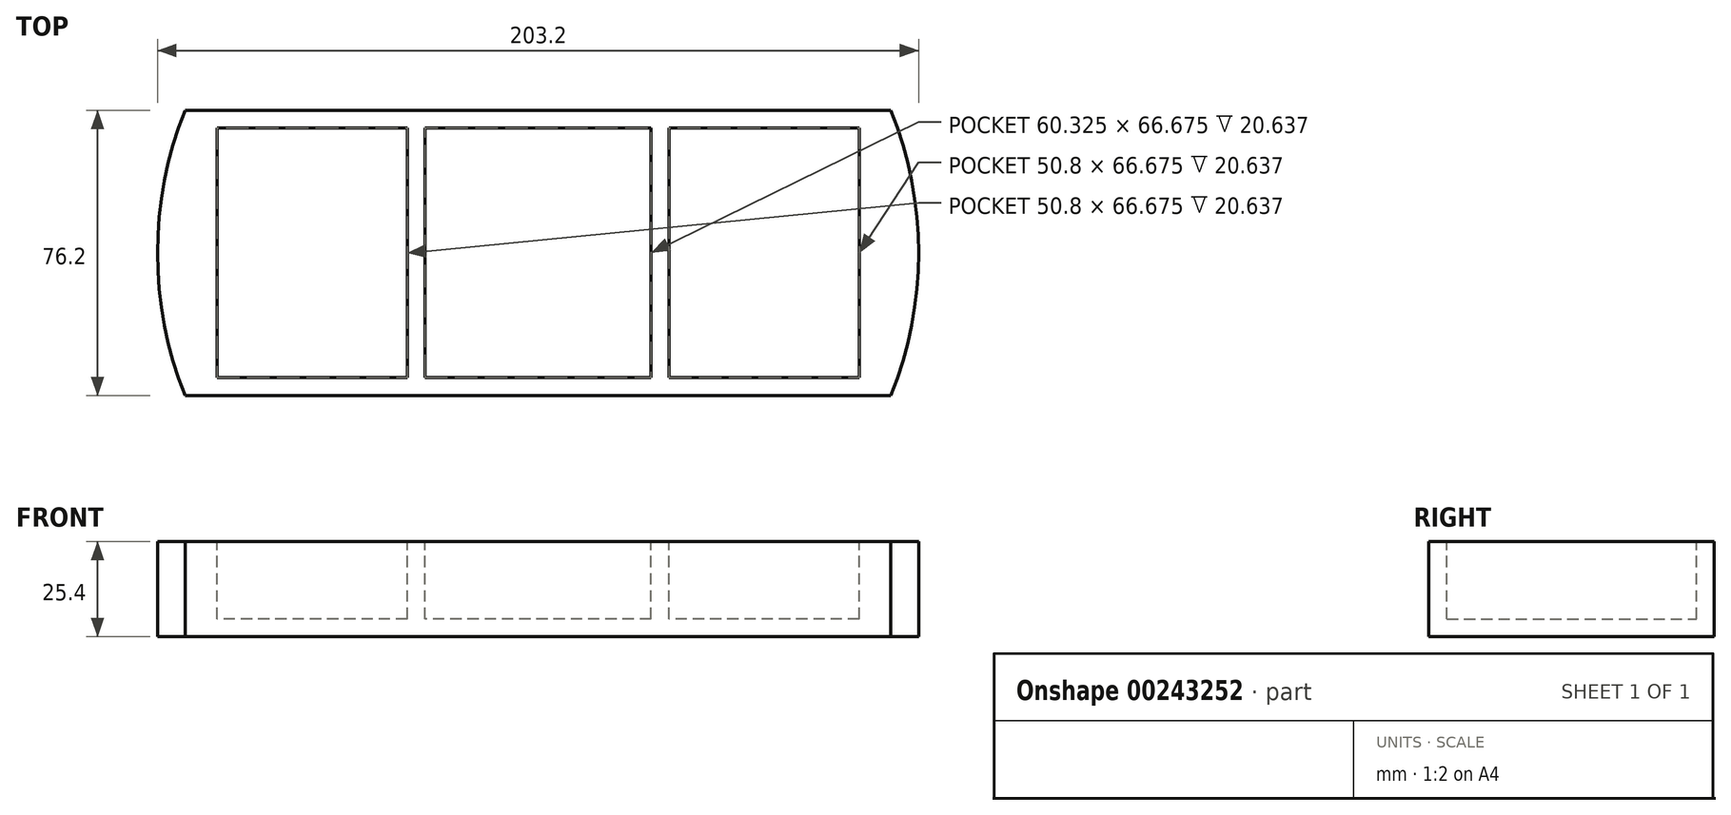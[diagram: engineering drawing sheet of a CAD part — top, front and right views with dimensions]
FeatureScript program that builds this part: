
annotation { "Feature Type Name" : "Feature", "Feature Type Description" : "" }
export const myFeature = defineFeature(function(context is Context, id is Id, definition is map)
    precondition{}
    {
        {
            var Q0;
            Q0=qCreatedBy(makeId("Front.planeOp"),FACE);
            var sketch = newSketch(context, id + "F0", { "sketchPlane" : qUnion([Q0])});
            skLineSegment(sketch, "E0.bottom", {"start": v(0, 0) * mm, "end": v(-203.2, 0) * mm});
            skLineSegment(sketch, "E0.top", {"start": v(0, 25.4) * mm, "end": v(-203.2, 25.4) * mm});
            skLineSegment(sketch, "E0.left", {"start": v(0, 0) * mm, "end": v(0, 25.4) * mm});
            skLineSegment(sketch, "E0.right", {"start": v(-203.2, 0) * mm, "end": v(-203.2, 25.4) * mm});
            skSolve(sketch);
        }
        {
            var Q0;
            Q0=makeQuery(id+"F0.imprint","IMPRINT",FACE,{"disambiguationData":[TD([[makeQuery(id+"F0.imprint","IMPRINT",EDGE,{"derivedFrom":sQuery(id+"F0.wireOp",EDGE,"E0.bottom")}),-1.0]])]});
            extrude(context, id + "F1", {"entities" : qUnion([Q0]), "depth" : 76.2 * mm});
        }
        {
            var Q0;
            Q0=makeQuery(id+"F1.opExtrude","SWEPT_FACE",FACE,{"disambiguationData":[OSD([sQuery(id+"F0.wireOp",EDGE,"E0.top")])]});
            var sketch = newSketch(context, id + "F2", { "sketchPlane" : qUnion([Q0])});
            skCircle(sketch, "E1", {"center": v(-101.6, -38.1) * mm, "radius": 101.6 * mm});
            skPoint(sketch, "E1.centerSnap0", {"position": v(-203.2, -38.1) * mm});
            skPoint(sketch, "E1.centerSnap1", {"position": v(-101.6, 0) * mm});
            skSolve(sketch);
        }
        {
            var Q0;
            {var subQ0=sQuery(id+"F2.wireOp",EDGE,"E1");var subQ1=sQuery(id+"F0.wireOp",EDGE,"E0.top");var subQ4=makeQuery(id+"F1.opExtrude","CAP_EDGE",EDGE,{"disambiguationData":[OSD([subQ1])],"isStart":false});var subQ5=makeQuery(id+"F2.imprint","INTERSECT",VERTEX,{"disambiguationData":[OD(1.0)],"derivedFrom":[subQ4,subQ0]});Q0=makeQuery(id+"F2.imprint","IMPRINT",FACE,{"disambiguationData":[TD([[makeQuery(id+"F2.imprint","IMPRINT",EDGE,{"disambiguationData":[TD([[subQ5,-1.0]])],"derivedFrom":subQ0}),-1.0]])]});}
            var Q1;
            {var subQ0=sQuery(id+"F2.wireOp",EDGE,"E1");var subQ1=sQuery(id+"F0.wireOp",EDGE,"E0.top");var subQ2=makeQuery(id+"F1.opExtrude","CAP_EDGE",EDGE,{"disambiguationData":[OSD([subQ1])],"isStart":true});var subQ3=makeQuery(id+"F2.imprint","INTERSECT",VERTEX,{"disambiguationData":[OD(0.0)],"derivedFrom":[subQ2,subQ0]});Q1=makeQuery(id+"F2.imprint","IMPRINT",FACE,{"disambiguationData":[TD([[makeQuery(id+"F2.imprint","IMPRINT",EDGE,{"disambiguationData":[TD([[subQ3,1.0]])],"derivedFrom":subQ0}),-1.0]])]});}
            var Q2;
            {var subQ0=sQuery(id+"F2.wireOp",EDGE,"E1");var subQ1=sQuery(id+"F0.wireOp",EDGE,"E0.top");var subQ2=makeQuery(id+"F1.opExtrude","CAP_EDGE",EDGE,{"disambiguationData":[OSD([subQ1])],"isStart":true});var subQ3=makeQuery(id+"F2.imprint","INTERSECT",VERTEX,{"disambiguationData":[OD(1.0)],"derivedFrom":[subQ2,subQ0]});Q2=makeQuery(id+"F2.imprint","IMPRINT",FACE,{"disambiguationData":[TD([[makeQuery(id+"F2.imprint","IMPRINT",EDGE,{"disambiguationData":[TD([[subQ3,-1.0]])],"derivedFrom":subQ0}),-1.0]])]});}
            var Q3;
            {var subQ0=sQuery(id+"F2.wireOp",EDGE,"E1");var subQ1=sQuery(id+"F0.wireOp",EDGE,"E0.top");var subQ4=makeQuery(id+"F1.opExtrude","CAP_EDGE",EDGE,{"disambiguationData":[OSD([subQ1])],"isStart":false});var subQ5=makeQuery(id+"F2.imprint","INTERSECT",VERTEX,{"disambiguationData":[OD(0.0)],"derivedFrom":[subQ4,subQ0]});Q3=makeQuery(id+"F2.imprint","IMPRINT",FACE,{"disambiguationData":[TD([[makeQuery(id+"F2.imprint","IMPRINT",EDGE,{"disambiguationData":[TD([[subQ5,1.0]])],"derivedFrom":subQ0}),-1.0]])]});}
            extrude(context, id + "F3", {"entities" : qUnion([Q0, Q1, Q2, Q3]), "operationType" : NewBodyOperationType.REMOVE, "oppositeDirection" : true, "depth" : 25.4 * mm});
        }
        {
            var Q0;
            Q0=makeQuery(id+"F1.opExtrude","SWEPT_FACE",FACE,{"disambiguationData":[OSD([sQuery(id+"F0.wireOp",EDGE,"E0.top")])]});
            var sketch = newSketch(context, id + "F4", { "sketchPlane" : qUnion([Q0])});
            skLineSegment(sketch, "E2", {"start": v(-203.2, -38.1) * mm, "end": v(-187.33, -38.1) * mm});
            skLineSegment(sketch, "E3", {"start": v(-187.33, -38.1) * mm, "end": v(-187.33, -71.44) * mm});
            skLineSegment(sketch, "E4", {"start": v(-187.33, -38.1) * mm, "end": v(-187.33, -4.76) * mm});
            skLineSegment(sketch, "E5", {"start": v(-187.33, -4.76) * mm, "end": v(-136.53, -4.76) * mm});
            skLineSegment(sketch, "E6", {"start": v(-136.53, -4.76) * mm, "end": v(-136.53, -71.44) * mm});
            skLineSegment(sketch, "E7", {"start": v(-136.53, -71.44) * mm, "end": v(-187.33, -71.44) * mm});
            skLineSegment(sketch, "E8", {"start": v(-136.53, -4.76) * mm, "end": v(-131.76, -4.76) * mm});
            skLineSegment(sketch, "E9", {"start": v(-131.76, -4.76) * mm, "end": v(-101.6, -4.76) * mm});
            skPoint(sketch, "E9.endSnap0", {"position": v(-101.6, 0) * mm});
            skLineSegment(sketch, "E10", {"start": v(-101.6, -4.76) * mm, "end": v(-101.6, -71.44) * mm});
            skLineSegment(sketch, "E11", {"start": v(-101.6, -71.44) * mm, "end": v(-131.76, -71.44) * mm});
            skLineSegment(sketch, "E12", {"start": v(-131.76, -71.44) * mm, "end": v(-131.76, -4.76) * mm});
            skLineSegment(sketch, "E13.MirrorCS", {"start": v(-66.67, -4.76) * mm, "end": v(-71.44, -4.76) * mm});
            skLineSegment(sketch, "E14.MirrorCS", {"start": v(-101.6, -71.44) * mm, "end": v(-71.44, -71.44) * mm});
            skLineSegment(sketch, "E15.MirrorCS", {"start": v(0, -38.1) * mm, "end": v(-15.87, -38.1) * mm});
            skLineSegment(sketch, "E16.MirrorCS", {"start": v(-15.87, -38.1) * mm, "end": v(-15.87, -4.76) * mm});
            skLineSegment(sketch, "E17.MirrorCS", {"start": v(-66.67, -4.76) * mm, "end": v(-66.67, -71.44) * mm});
            skLineSegment(sketch, "E18.MirrorCS", {"start": v(-15.87, -4.76) * mm, "end": v(-66.67, -4.76) * mm});
            skLineSegment(sketch, "E19.MirrorCS", {"start": v(-71.44, -4.76) * mm, "end": v(-101.6, -4.76) * mm});
            skLineSegment(sketch, "E20.MirrorCS", {"start": v(-15.87, -38.1) * mm, "end": v(-15.87, -71.44) * mm});
            skLineSegment(sketch, "E21.MirrorCS", {"start": v(-66.67, -71.44) * mm, "end": v(-15.87, -71.44) * mm});
            skLineSegment(sketch, "E22.MirrorCS", {"start": v(-71.44, -71.44) * mm, "end": v(-71.44, -4.76) * mm});
            skSolve(sketch);
        }
        {
            var Q0;
            Q0=makeQuery(id+"F4.imprint","IMPRINT",FACE,{"disambiguationData":[TD([[makeQuery(id+"F4.imprint","IMPRINT",EDGE,{"derivedFrom":sQuery(id+"F4.wireOp",EDGE,"E3")}),1.0]])]});
            var Q1;
            Q1=makeQuery(id+"F4.imprint","IMPRINT",FACE,{"disambiguationData":[TD([[makeQuery(id+"F4.imprint","IMPRINT",EDGE,{"derivedFrom":sQuery(id+"F4.wireOp",EDGE,"E16.MirrorCS")}),1.0]])]});
            var Q2;
            Q2=makeQuery(id+"F4.imprint","IMPRINT",FACE,{"disambiguationData":[TD([[makeQuery(id+"F4.imprint","IMPRINT",EDGE,{"derivedFrom":sQuery(id+"F4.wireOp",EDGE,"E10")}),1.0]])]});
            var Q3;
            Q3=makeQuery(id+"F4.imprint","IMPRINT",FACE,{"disambiguationData":[TD([[makeQuery(id+"F4.imprint","IMPRINT",EDGE,{"derivedFrom":sQuery(id+"F4.wireOp",EDGE,"E9")}),-1.0]])]});
            extrude(context, id + "F5", {"entities" : qUnion([Q0, Q1, Q2, Q3]), "operationType" : NewBodyOperationType.REMOVE, "oppositeDirection" : true, "depth" : 20.64 * mm});
        }
    });
